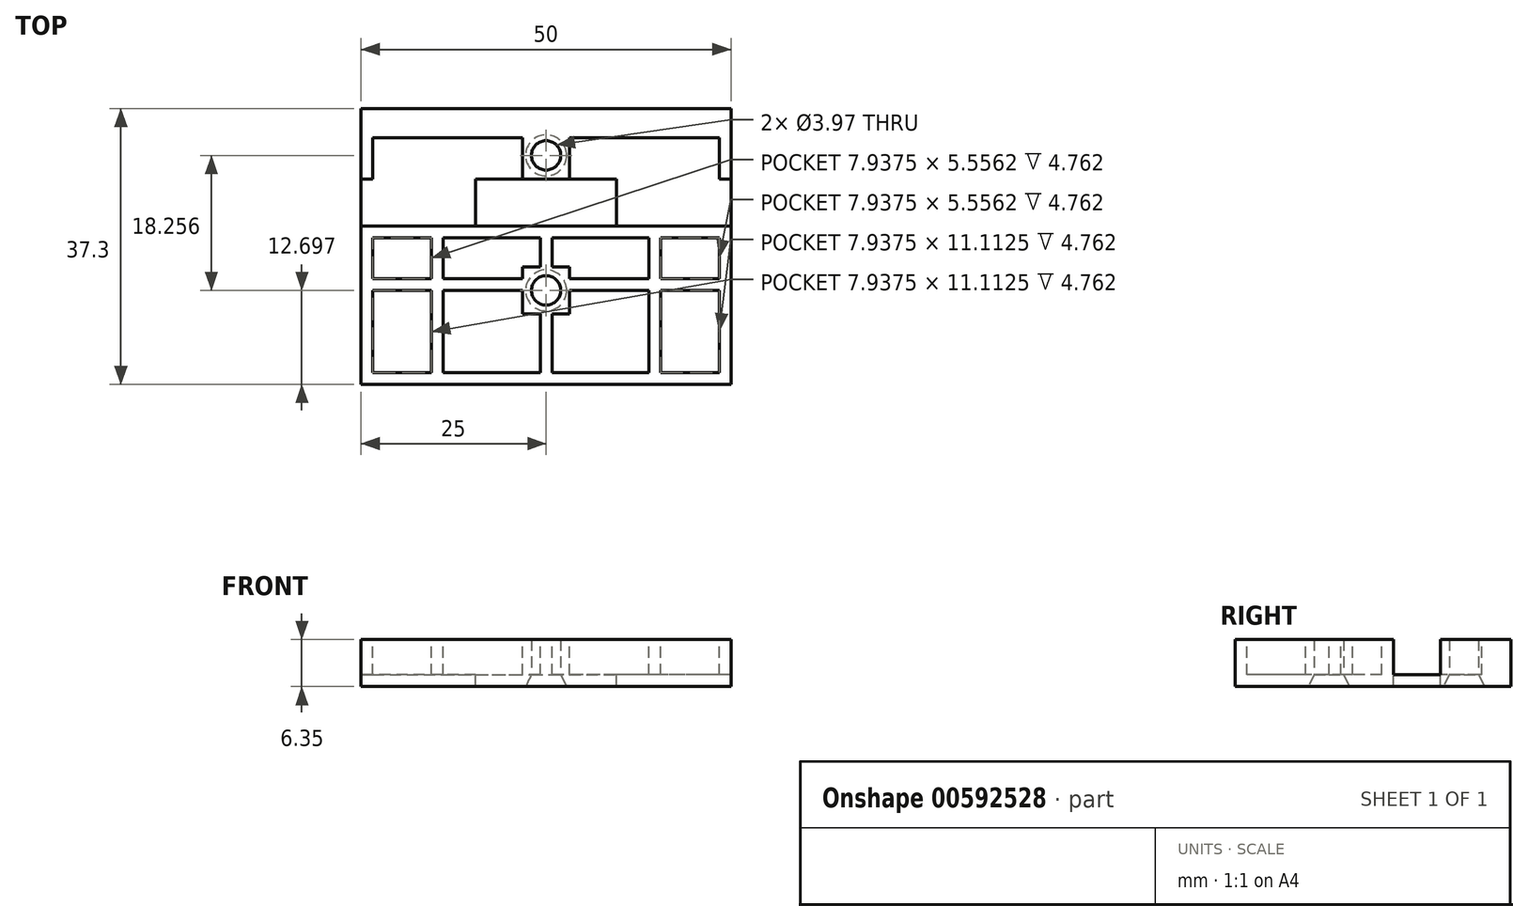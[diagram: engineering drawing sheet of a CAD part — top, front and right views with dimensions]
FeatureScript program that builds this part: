
annotation { "Feature Type Name" : "Feature", "Feature Type Description" : "" }
export const myFeature = defineFeature(function(context is Context, id is Id, definition is map)
    precondition{}
    {
        {
            var Q0;
            Q0=qCreatedBy(makeId("Top.planeOp"),FACE);
            var sketch = newSketch(context, id + "F0", { "sketchPlane" : qUnion([Q0])});
            skLineSegment(sketch, "E0.bottom", {"start": v(25, 18.65) * mm, "end": v(-25, 18.65) * mm});
            skLineSegment(sketch, "E0.top", {"start": v(25, -18.65) * mm, "end": v(-25, -18.65) * mm});
            skLineSegment(sketch, "E0.left", {"start": v(25, 18.65) * mm, "end": v(25, -18.65) * mm});
            skLineSegment(sketch, "E0.right", {"start": v(-25, 18.65) * mm, "end": v(-25, -18.65) * mm});
            skPoint(sketch, "E0.middle", {"position": v(0, 0) * mm});
            skCircle(sketch, "E1", {"center": v(0, 12.3) * mm, "radius": 1.98 * mm});
            skCircle(sketch, "E2", {"center": v(0, -5.95) * mm, "radius": 1.98 * mm});
            skLineSegment(sketch, "E3.bottom", {"start": v(9.52, 8.73) * mm, "end": v(-9.53, 8.73) * mm});
            skLineSegment(sketch, "E3.top", {"start": v(9.53, 3.17) * mm, "end": v(-9.53, 3.17) * mm});
            skLineSegment(sketch, "E3.left", {"start": v(9.52, 8.73) * mm, "end": v(9.52, 3.17) * mm});
            skLineSegment(sketch, "E3.right", {"start": v(-9.53, 8.73) * mm, "end": v(-9.53, 3.17) * mm});
            skPoint(sketch, "E3.middle", {"position": v(0, 5.95) * mm});
            skSolve(sketch);
        }
        {
            var Q0;
            Q0=makeQuery(id+"F0.imprint","IMPRINT",FACE,{"disambiguationData":[TD([[makeQuery(id+"F0.imprint","IMPRINT",EDGE,{"derivedFrom":sQuery(id+"F0.wireOp",EDGE,"E0.bottom")}),1.0]])]});
            extrude(context, id + "F1", {"entities" : qUnion([Q0]), "depth" : 6.35 * mm, "offsetDistance" : 25.4 * mm});
        }
        {
            var Q0;
            Q0=makeQuery(id+"F1.opExtrude","CAP_FACE",FACE,{"disambiguationData":[OSD([sQuery(id+"F0.wireOp",EDGE,"E0.bottom"),sQuery(id+"F0.wireOp",EDGE,"E0.top"),sQuery(id+"F0.wireOp",EDGE,"E0.left"),sQuery(id+"F0.wireOp",EDGE,"E0.right"),sQuery(id+"F0.wireOp",EDGE,"E1"),sQuery(id+"F0.wireOp",EDGE,"E2"),sQuery(id+"F0.wireOp",EDGE,"E3.bottom"),sQuery(id+"F0.wireOp",EDGE,"E3.top"),sQuery(id+"F0.wireOp",EDGE,"E3.left"),sQuery(id+"F0.wireOp",EDGE,"E3.right")])],"isStart":false});
            var sketch = newSketch(context, id + "F2", { "sketchPlane" : qUnion([Q0])});
            skLineSegment(sketch, "E4.bottom", {"start": v(-23.42, 14.68) * mm, "end": v(-3.18, 14.68) * mm});
            skLineSegment(sketch, "E4.top", {"start": v(-23.42, 2.78) * mm, "end": v(0, 2.78) * mm});
            skLineSegment(sketch, "E4.left", {"start": v(-23.42, 14.68) * mm, "end": v(-23.42, 9.13) * mm});
            skLineSegment(sketch, "E5.bottom", {"start": v(-23.42, 1.2) * mm, "end": v(-15.48, 1.2) * mm});
            skLineSegment(sketch, "E5.top", {"start": v(-23.42, -4.37) * mm, "end": v(-15.48, -4.37) * mm});
            skLineSegment(sketch, "E5.left", {"start": v(-23.42, 1.2) * mm, "end": v(-23.42, -4.37) * mm});
            skLineSegment(sketch, "E5.right", {"start": v(-15.48, 1.2) * mm, "end": v(-15.48, -4.37) * mm});
            skLineSegment(sketch, "E6.bottom", {"start": v(-13.9, 1.2) * mm, "end": v(-0.8, 1.2) * mm});
            skLineSegment(sketch, "E6.top", {"start": v(-13.9, -4.37) * mm, "end": v(-3.18, -4.37) * mm});
            skLineSegment(sketch, "E6.left", {"start": v(-13.9, 1.2) * mm, "end": v(-13.9, -4.37) * mm});
            skLineSegment(sketch, "E6.right", {"start": v(-0.8, 1.2) * mm, "end": v(-0.8, -2.78) * mm});
            skLineSegment(sketch, "E7.bottom", {"start": v(-23.42, -5.95) * mm, "end": v(-15.48, -5.95) * mm});
            skLineSegment(sketch, "E7.top", {"start": v(-23.42, -17.07) * mm, "end": v(-15.48, -17.07) * mm});
            skLineSegment(sketch, "E7.left", {"start": v(-23.42, -5.95) * mm, "end": v(-23.42, -17.07) * mm});
            skLineSegment(sketch, "E7.right", {"start": v(-15.48, -5.95) * mm, "end": v(-15.48, -17.07) * mm});
            skLineSegment(sketch, "E8.bottom", {"start": v(-13.9, -5.95) * mm, "end": v(-3.18, -5.95) * mm});
            skLineSegment(sketch, "E8.top", {"start": v(-13.9, -17.07) * mm, "end": v(-0.8, -17.07) * mm});
            skLineSegment(sketch, "E8.left", {"start": v(-13.9, -5.95) * mm, "end": v(-13.9, -17.07) * mm});
            skLineSegment(sketch, "E8.right", {"start": v(-0.8, -9.13) * mm, "end": v(-0.8, -17.07) * mm});
            skLineSegment(sketch, "E9.bottom", {"start": v(-0.8, -2.78) * mm, "end": v(-3.17, -2.78) * mm});
            skLineSegment(sketch, "E9.top", {"start": v(-0.8, -9.13) * mm, "end": v(-3.18, -9.13) * mm});
            skLineSegment(sketch, "E9.right", {"start": v(-3.18, -2.78) * mm, "end": v(-3.18, -4.37) * mm});
            skPoint(sketch, "E9.middle", {"position": v(0, -5.95) * mm});
            skPoint(sketch, "E10.top.end.orphan", {"position": v(0, 2.78) * mm});
            skLineSegment(sketch, "E11.right", {"start": v(-3.17, 14.68) * mm, "end": v(-3.17, 9.13) * mm});
            skPoint(sketch, "E11.middle", {"position": v(0, 12.3) * mm});
            skPoint(sketch, "E12.right.end.orphan", {"position": v(0, 16.27) * mm});
            skLineSegment(sketch, "E13", {"start": v(-25, 2.78) * mm, "end": v(-25, 9.13) * mm});
            skLineSegment(sketch, "E14", {"start": v(-25, 9.13) * mm, "end": v(-23.42, 9.13) * mm});
            skLineSegment(sketch, "E15", {"start": v(-23.42, 2.78) * mm, "end": v(-25, 2.78) * mm});
            skPoint(sketch, "E16.start.orphan", {"position": v(3.17, 18.65) * mm});
            skPoint(sketch, "E17.orphan", {"position": v(3.18, 9.13) * mm});
            skLineSegment(sketch, "E18.trimOffspring", {"start": v(-3.18, -5.95) * mm, "end": v(-3.18, -9.13) * mm});
            skPoint(sketch, "E19.orphan", {"position": v(-0.8, -4.37) * mm});
            skPoint(sketch, "E9.left.end.orphan", {"position": v(3.17, -9.13) * mm});
            skPoint(sketch, "E9.left.start.orphan", {"position": v(3.17, -2.78) * mm});
            skLineSegment(sketch, "E20.MirrorCS", {"start": v(3.18, -2.78) * mm, "end": v(3.18, -4.37) * mm});
            skLineSegment(sketch, "E21.MirrorCS", {"start": v(0.8, -2.78) * mm, "end": v(3.17, -2.78) * mm});
            skLineSegment(sketch, "E22.MirrorCS", {"start": v(3.18, -5.95) * mm, "end": v(3.18, -9.13) * mm});
            skLineSegment(sketch, "E23.MirrorCS", {"start": v(23.42, 2.78) * mm, "end": v(25, 2.78) * mm});
            skLineSegment(sketch, "E24.MirrorCS", {"start": v(25, 9.13) * mm, "end": v(23.42, 9.13) * mm});
            skLineSegment(sketch, "E25.MirrorCS", {"start": v(0.8, -9.13) * mm, "end": v(3.18, -9.13) * mm});
            skLineSegment(sketch, "E26.MirrorCS", {"start": v(3.17, 14.68) * mm, "end": v(3.17, 9.13) * mm});
            skLineSegment(sketch, "E27.MirrorCS", {"start": v(23.42, 1.2) * mm, "end": v(15.48, 1.2) * mm});
            skLineSegment(sketch, "E28.MirrorCS", {"start": v(23.42, -4.37) * mm, "end": v(15.48, -4.37) * mm});
            skLineSegment(sketch, "E29.MirrorCS", {"start": v(15.48, 1.2) * mm, "end": v(15.48, -4.37) * mm});
            skLineSegment(sketch, "E30.MirrorCS", {"start": v(13.9, 1.2) * mm, "end": v(13.9, -4.37) * mm});
            skLineSegment(sketch, "E31.MirrorCS", {"start": v(0.8, -9.13) * mm, "end": v(0.8, -17.07) * mm});
            skLineSegment(sketch, "E32.MirrorCS", {"start": v(13.9, -4.37) * mm, "end": v(3.18, -4.37) * mm});
            skLineSegment(sketch, "E33.MirrorCS", {"start": v(0.8, 1.2) * mm, "end": v(0.8, -2.78) * mm});
            skLineSegment(sketch, "E34.MirrorCS", {"start": v(13.9, -5.95) * mm, "end": v(13.9, -17.07) * mm});
            skLineSegment(sketch, "E35.MirrorCS", {"start": v(13.9, -5.95) * mm, "end": v(3.18, -5.95) * mm});
            skPoint(sketch, "E36.MirrorP", {"position": v(0.8, -4.37) * mm});
            skLineSegment(sketch, "E37.MirrorCS", {"start": v(15.48, -5.95) * mm, "end": v(15.48, -17.07) * mm});
            skLineSegment(sketch, "E38.MirrorCS", {"start": v(13.9, 1.2) * mm, "end": v(0.8, 1.2) * mm});
            skLineSegment(sketch, "E39.MirrorCS", {"start": v(23.42, -5.95) * mm, "end": v(15.48, -5.95) * mm});
            skLineSegment(sketch, "E40.MirrorCS", {"start": v(23.42, 1.2) * mm, "end": v(23.42, -4.37) * mm});
            skLineSegment(sketch, "E41.MirrorCS", {"start": v(23.42, 2.78) * mm, "end": v(0, 2.78) * mm});
            skLineSegment(sketch, "E42.MirrorCS", {"start": v(23.42, 14.68) * mm, "end": v(23.42, 9.13) * mm});
            skLineSegment(sketch, "E43.MirrorCS", {"start": v(25, 2.78) * mm, "end": v(25, 9.13) * mm});
            skLineSegment(sketch, "E44.MirrorCS", {"start": v(23.42, -5.95) * mm, "end": v(23.42, -17.07) * mm});
            skLineSegment(sketch, "E45.MirrorCS", {"start": v(23.42, -17.07) * mm, "end": v(15.48, -17.07) * mm});
            skLineSegment(sketch, "E46.MirrorCS", {"start": v(23.42, 14.68) * mm, "end": v(3.18, 14.68) * mm});
            skLineSegment(sketch, "E47.MirrorCS", {"start": v(13.9, -17.07) * mm, "end": v(0.8, -17.07) * mm});
            skPoint(sketch, "E11.top.start.orphan", {"position": v(0, 10.32) * mm});
            skLineSegment(sketch, "E48", {"start": v(-3.18, 9.13) * mm, "end": v(3.18, 9.13) * mm});
            skSolve(sketch);
        }
        {
            var Q0;
            Q0 = qSketchRegion(id + "F2", true);
            extrude(context, id + "F3", {"entities" : qUnion([Q0]), "operationType" : NewBodyOperationType.REMOVE, "oppositeDirection" : true, "depth" : 4.76 * mm, "offsetDistance" : 25.4 * mm});
        }
        {
            var Q0;
            Q0=makeQuery(id+"F1.opExtrude","CAP_FACE",FACE,{"disambiguationData":[OSD([sQuery(id+"F0.wireOp",EDGE,"E0.bottom"),sQuery(id+"F0.wireOp",EDGE,"E0.top"),sQuery(id+"F0.wireOp",EDGE,"E0.left"),sQuery(id+"F0.wireOp",EDGE,"E0.right"),sQuery(id+"F0.wireOp",EDGE,"E1"),sQuery(id+"F0.wireOp",EDGE,"E2"),sQuery(id+"F0.wireOp",EDGE,"E3.bottom"),sQuery(id+"F0.wireOp",EDGE,"E3.top"),sQuery(id+"F0.wireOp",EDGE,"E3.left"),sQuery(id+"F0.wireOp",EDGE,"E3.right")])],"isStart":true});
            cPlane(context, id + "F4", {"entities" : qUnion([Q0]), "cplaneType" : CPlaneType.OFFSET, "offset" : 1.59 * mm, "oppositeDirection" : true, "width" : 152.4 * mm, "height" : 152.4 * mm});
        }
        {
            var Q0;
            Q0=qCreatedBy(id+"F4.planeOp",FACE);
            var sketch = newSketch(context, id + "F5", { "sketchPlane" : qUnion([Q0])});
            skCircle(sketch, "E49", {"center": v(0, -12.3) * mm, "radius": 1.98 * mm});
            skSolve(sketch);
        }
        {
            var Q0;
            Q0=makeQuery(id+"F1.opExtrude","CAP_FACE",FACE,{"disambiguationData":[OSD([sQuery(id+"F0.wireOp",EDGE,"E0.bottom"),sQuery(id+"F0.wireOp",EDGE,"E0.top"),sQuery(id+"F0.wireOp",EDGE,"E0.left"),sQuery(id+"F0.wireOp",EDGE,"E0.right"),sQuery(id+"F0.wireOp",EDGE,"E1"),sQuery(id+"F0.wireOp",EDGE,"E2"),sQuery(id+"F0.wireOp",EDGE,"E3.bottom"),sQuery(id+"F0.wireOp",EDGE,"E3.top"),sQuery(id+"F0.wireOp",EDGE,"E3.left"),sQuery(id+"F0.wireOp",EDGE,"E3.right")])],"isStart":true});
            var sketch = newSketch(context, id + "F6", { "sketchPlane" : qUnion([Q0])});
            skCircle(sketch, "E50", {"center": v(0, -12.3) * mm, "radius": 2.78 * mm});
            skSolve(sketch);
        }
        {
            var Q1;
            Q1 = qSketchRegion(id + "F5", true);
            var Q2;
            Q2 = qSketchRegion(id + "F6", true);
            loft(context, id + "F7", {"operationType" : NewBodyOperationType.REMOVE, "sheetProfilesArray" : [{ "sheetProfileEntities" : qUnion([Q1]) }, { "sheetProfileEntities" : qUnion([Q2]) }]});
        }
        {
            var Q0;
            Q0=makeQuery(id+"F1.opExtrude","CAP_FACE",FACE,{"disambiguationData":[OSD([sQuery(id+"F0.wireOp",EDGE,"E0.bottom"),sQuery(id+"F0.wireOp",EDGE,"E0.top"),sQuery(id+"F0.wireOp",EDGE,"E0.left"),sQuery(id+"F0.wireOp",EDGE,"E0.right"),sQuery(id+"F0.wireOp",EDGE,"E1"),sQuery(id+"F0.wireOp",EDGE,"E2"),sQuery(id+"F0.wireOp",EDGE,"E3.bottom"),sQuery(id+"F0.wireOp",EDGE,"E3.top"),sQuery(id+"F0.wireOp",EDGE,"E3.left"),sQuery(id+"F0.wireOp",EDGE,"E3.right")])],"isStart":true});
            var sketch = newSketch(context, id + "F8", { "sketchPlane" : qUnion([Q0])});
            skCircle(sketch, "E51", {"center": v(0, 5.95) * mm, "radius": 2.78 * mm});
            skSolve(sketch);
        }
        {
            var Q0;
            Q0=qCreatedBy(id+"F4.planeOp",FACE);
            var sketch = newSketch(context, id + "F9", { "sketchPlane" : qUnion([Q0])});
            skCircle(sketch, "E52", {"center": v(0, 5.95) * mm, "radius": 1.98 * mm});
            skSolve(sketch);
        }
        {
            var Q1;
            Q1 = qSketchRegion(id + "F8", true);
            var Q2;
            Q2 = qSketchRegion(id + "F9", true);
            loft(context, id + "F10", {"operationType" : NewBodyOperationType.REMOVE, "sheetProfilesArray" : [{ "sheetProfileEntities" : qUnion([Q1]) }, { "sheetProfileEntities" : qUnion([Q2]) }]});
        }
        {
            var Q0;
            Q0=makeQuery(id+"F3.boolean.opBoolean","COPY",FACE,{"derivedFrom":makeQuery(id+"F3.opExtrude","CAP_FACE",FACE,{"disambiguationData":[OSD([sQuery(id+"F2.wireOp",EDGE,"E4.bottom"),sQuery(id+"F2.wireOp",EDGE,"E4.top"),sQuery(id+"F2.wireOp",EDGE,"E4.left"),sQuery(id+"F2.wireOp",EDGE,"E11.right"),sQuery(id+"F2.wireOp",EDGE,"E13"),sQuery(id+"F2.wireOp",EDGE,"E14"),sQuery(id+"F2.wireOp",EDGE,"E15"),sQuery(id+"F2.wireOp",EDGE,"E23.MirrorCS"),sQuery(id+"F2.wireOp",EDGE,"E24.MirrorCS"),sQuery(id+"F2.wireOp",EDGE,"E26.MirrorCS"),sQuery(id+"F2.wireOp",EDGE,"E41.MirrorCS"),sQuery(id+"F2.wireOp",EDGE,"E42.MirrorCS"),sQuery(id+"F2.wireOp",EDGE,"E43.MirrorCS"),sQuery(id+"F2.wireOp",EDGE,"E46.MirrorCS"),sQuery(id+"F2.wireOp",EDGE,"E48")])],"isStart":false})});
            var sketch = newSketch(context, id + "F11", { "sketchPlane" : qUnion([Q0])});
            skLineSegment(sketch, "E53.bottom", {"start": v(-9.52, 2.78) * mm, "end": v(9.52, 2.78) * mm});
            skLineSegment(sketch, "E53.top", {"start": v(-9.52, 9.13) * mm, "end": v(9.52, 9.13) * mm});
            skLineSegment(sketch, "E53.left", {"start": v(-9.53, 2.78) * mm, "end": v(-9.53, 9.13) * mm});
            skLineSegment(sketch, "E53.right", {"start": v(9.52, 2.78) * mm, "end": v(9.52, 9.13) * mm});
            skSolve(sketch);
        }
        {
            var Q0;
            Q0 = qSketchRegion(id + "F11", true);
            extrude(context, id + "F12", {"entities" : qUnion([Q0]), "operationType" : NewBodyOperationType.REMOVE, "oppositeDirection" : true, "depth" : 25.4 * mm, "offsetDistance" : 25.4 * mm});
        }
    });
